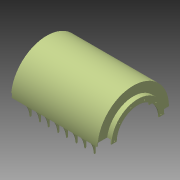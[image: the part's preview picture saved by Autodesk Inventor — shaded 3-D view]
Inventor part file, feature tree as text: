
AUTODESK INVENTOR PART (.ipt)
format: ipt  version: 2015 (Build 190159000, 159)  size: 359,936 bytes
history: native  units: mm
features: sketch x6, extrude x5, revolve x1, pattern_circular x1
ambient origin geometry x8: Origin, YZ Plane, XZ Plane, XY Plane, X Axis, Y Axis, Z Axis, Center Point
bodies: 实体1 (feature_tree)
feature tree (13):
  revolve  "旋转1"  [1 undecoded]
  extrude  "拉伸1"  Depth=35.0mm
  pattern_circular  "环形阵列1"  Count=28  [1 undecoded]
  extrude  "拉伸2"  Depth=30.0mm
  extrude  "拉伸3"  Depth=235.0mm
  extrude  "拉伸4"  Depth=560.0mm
  extrude  "拉伸5"  Depth=5.0mm
  sketch  "草图1"  dims[d0=100.0mm d1=25.0mm]
  sketch  "草图2"  dims[d2=100.0mm d4=360.0deg d6=35.0mm]
  sketch  "草图3"  dims[d7=2.5mm]
  sketch  "草图4"  dims[d8=5.0mm d9=280.0mm]
  sketch  "草图5"  dims[d10=5.0mm d11=30.0mm]
  sketch  "草图6"  dims[d12=5.0mm d13=235.0mm d14=560.0mm d15=5.0mm d16=5.0mm d17=35.0mm d18=5.0mm d19=5.0mm d20=3.0mm d21=210.0mm d22=3.0mm d23=60.0mm d24=55.0mm d25=3.0mm d26=3.0mm d27=3.0mm d28=3.0mm d29=3.0mm d30=3.0mm d31=120.0mm d32=60.0mm d33=120.0mm d34=60.0mm d35=120.0mm d36=60.0mm d37=180.0deg d38=5.0mm d39=153.0mm d40=10.0mm d41=10.0mm d42=0.0mm d43=60.0mm d44=30.10693mm d46=100.0mm d47=0.0mm d48=10.0mm d49=80.0mm d50=0.0mm d51=80.0mm d52=0.0mm d53=25.0mm d54=0.0mm]
note: 2 required parameter values undecoded (feature->parameter linkage not recoverable at this tier; creation-order binding heuristic only, values carry confidence <= 0.55)